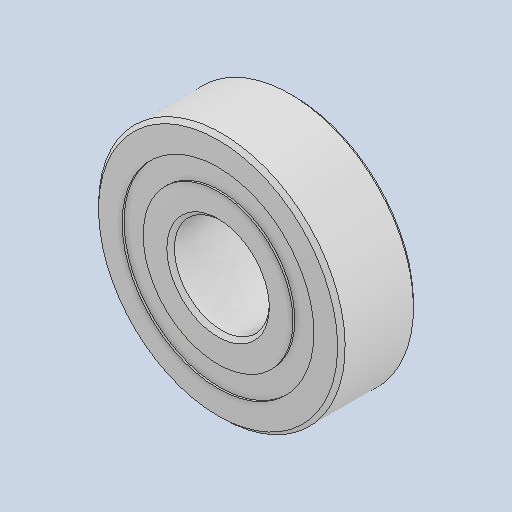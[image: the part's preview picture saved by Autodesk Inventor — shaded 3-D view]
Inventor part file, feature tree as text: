
AUTODESK INVENTOR PART (.ipt)
format: ipt  version: 2023 (Build 270158030, 158C)  size: 492,032 bytes
history: mixed  units: in
note: dims shown in document units (in); Inventor stores cm internally (conversion verified against a paired STEP export)
features: other x9, revolve x5, imported_body x1
ambient origin geometry x8: Origin, YZ Plane, XZ Plane, XY Plane, X Axis, Y Axis, Z Axis, Center Point
bodies: Solid1 (imported_parasolid), Solid2 (imported_parasolid), Solid3 (imported_parasolid), Solid4 (imported_parasolid), Solid5 (imported_parasolid), Solid6 (imported_parasolid), Solid7 (imported_parasolid), Solid8 (imported_parasolid), Solid9 (imported_parasolid), Solid10 (imported_parasolid), Solid11 (imported_parasolid), Solid12 (imported_parasolid), Solid13 (imported_parasolid), Solid14 (imported_parasolid)
feature tree (15):
  revolve  "Revolve6"  [1 undecoded]
  revolve  "Revolve3"  [1 undecoded]
  revolve  "Revolve4"  [1 undecoded]
  other  "CirPattern1[1]"
  other  "CirPattern1[2]"
  other  "CirPattern1[3]"
  other  "CirPattern1[4]"
  other  "CirPattern1[5]"
  other  "CirPattern1[6]"
  other  "CirPattern1[7]"
  other  "CirPattern1[8]"
  other  "CirPattern1[9]"
  revolve  "Revolve5[1]"  [1 undecoded]
  revolve  "Revolve5[2]"  [1 undecoded]
  imported_body  NMx_Import_Brep_tag  [imported B-rep: ~34 faces, bbox_mm=[0.0, 8.0, 8.0]]
note: 5 required parameter values undecoded (feature->parameter linkage not recoverable at this tier; creation-order binding heuristic only, values carry confidence <= 0.55)
